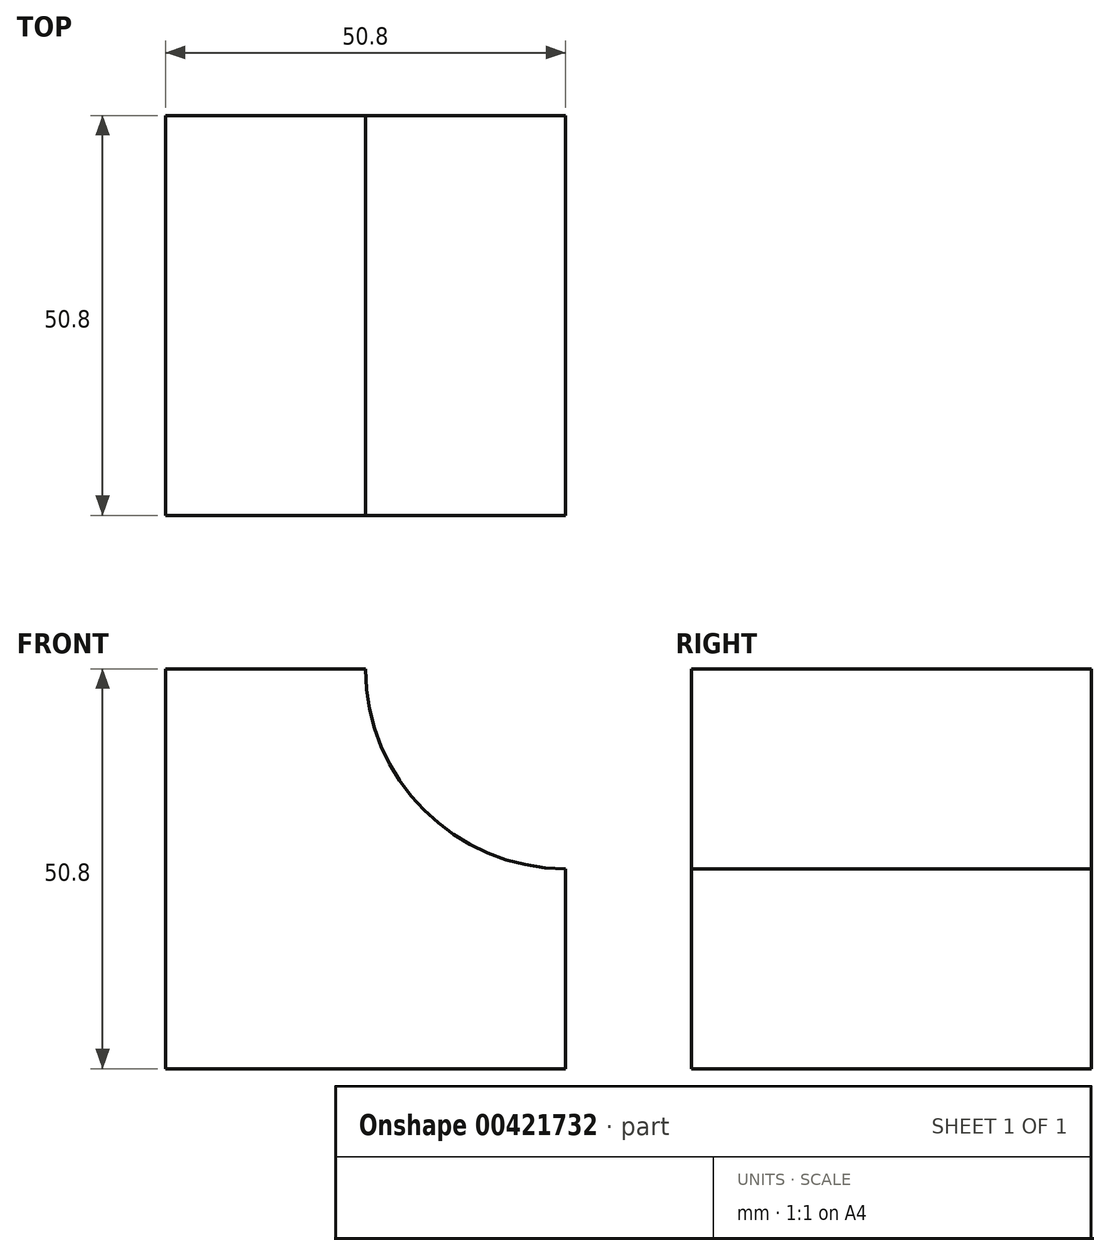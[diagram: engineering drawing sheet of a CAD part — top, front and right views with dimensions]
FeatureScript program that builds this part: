
annotation { "Feature Type Name" : "Feature", "Feature Type Description" : "" }
export const myFeature = defineFeature(function(context is Context, id is Id, definition is map)
    precondition{}
    {
        {
            var Q0;
            Q0=qCreatedBy(makeId("Front.planeOp"),FACE);
            var sketch = newSketch(context, id + "F0", { "sketchPlane" : qUnion([Q0])});
            skLineSegment(sketch, "E0", {"start": v(0, 0) * mm, "end": v(-50.8, 0) * mm});
            skLineSegment(sketch, "E1", {"start": v(-50.8, 0) * mm, "end": v(-50.8, 50.8) * mm});
            skLineSegment(sketch, "E2", {"start": v(-50.8, 50.8) * mm, "end": v(-25.4, 50.8) * mm});
            skLineSegment(sketch, "E3", {"start": v(-25.4, 50.8) * mm, "end": v(-25.4, 25.4) * mm});
            skLineSegment(sketch, "E4", {"start": v(-25.4, 25.4) * mm, "end": v(0, 25.4) * mm});
            skLineSegment(sketch, "E5", {"start": v(0, 25.4) * mm, "end": v(0, 0) * mm});
            skArc(sketch, "E6", {"start": v(-25.4, 50.8) * mm, "mid": v(-17.96, 32.84) * mm, "end": v(0, 25.4) * mm});
            skSolve(sketch);
        }
        {
            var Q0;
            Q0 = qSketchRegion(id + "F0", true);
            extrude(context, id + "F1", {"entities" : qUnion([Q0]), "depth" : 50.8 * mm});
        }
    });
